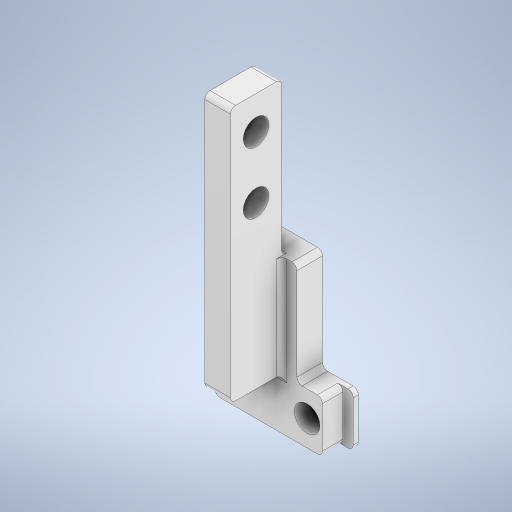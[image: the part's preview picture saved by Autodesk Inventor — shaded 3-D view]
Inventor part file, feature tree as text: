
AUTODESK INVENTOR PART (.ipt)
format: ipt  version: 2024.3 (Build 283343000, 343)  size: 365,056 bytes
history: native  units: mm
features: sketch x5, extrude x4, fillet x2, hole x1, projected_geometry x1
ambient origin geometry x8: Origin, YZ Plane, XZ Plane, XY Plane, X Axis, Y Axis, Z Axis, Center Point
bodies: Body1 (feature_tree)
feature tree (13):
  extrude  "押し出し4"  Depth=5.0mm
  extrude  "押し出し5"  Depth=5.0mm
  hole  "穴3"  [1 undecoded]
  extrude  "押し出し6"  Depth=5.0mm
  fillet  "フィレット4"  Radius=15.0mm
  extrude  "押し出し7"  Depth=5.0mm
  fillet  "フィレット5"  Radius=5.0mm
  sketch  "スケッチ6"
  sketch  "スケッチ7"
  sketch  "スケッチ8"
  sketch  "スケッチ9"
  sketch  "スケッチ10"
  projected_geometry  "投影ループ1"
note: 1 required parameter value undecoded (feature->parameter linkage not recoverable at this tier; creation-order binding heuristic only, values carry confidence <= 0.55)
